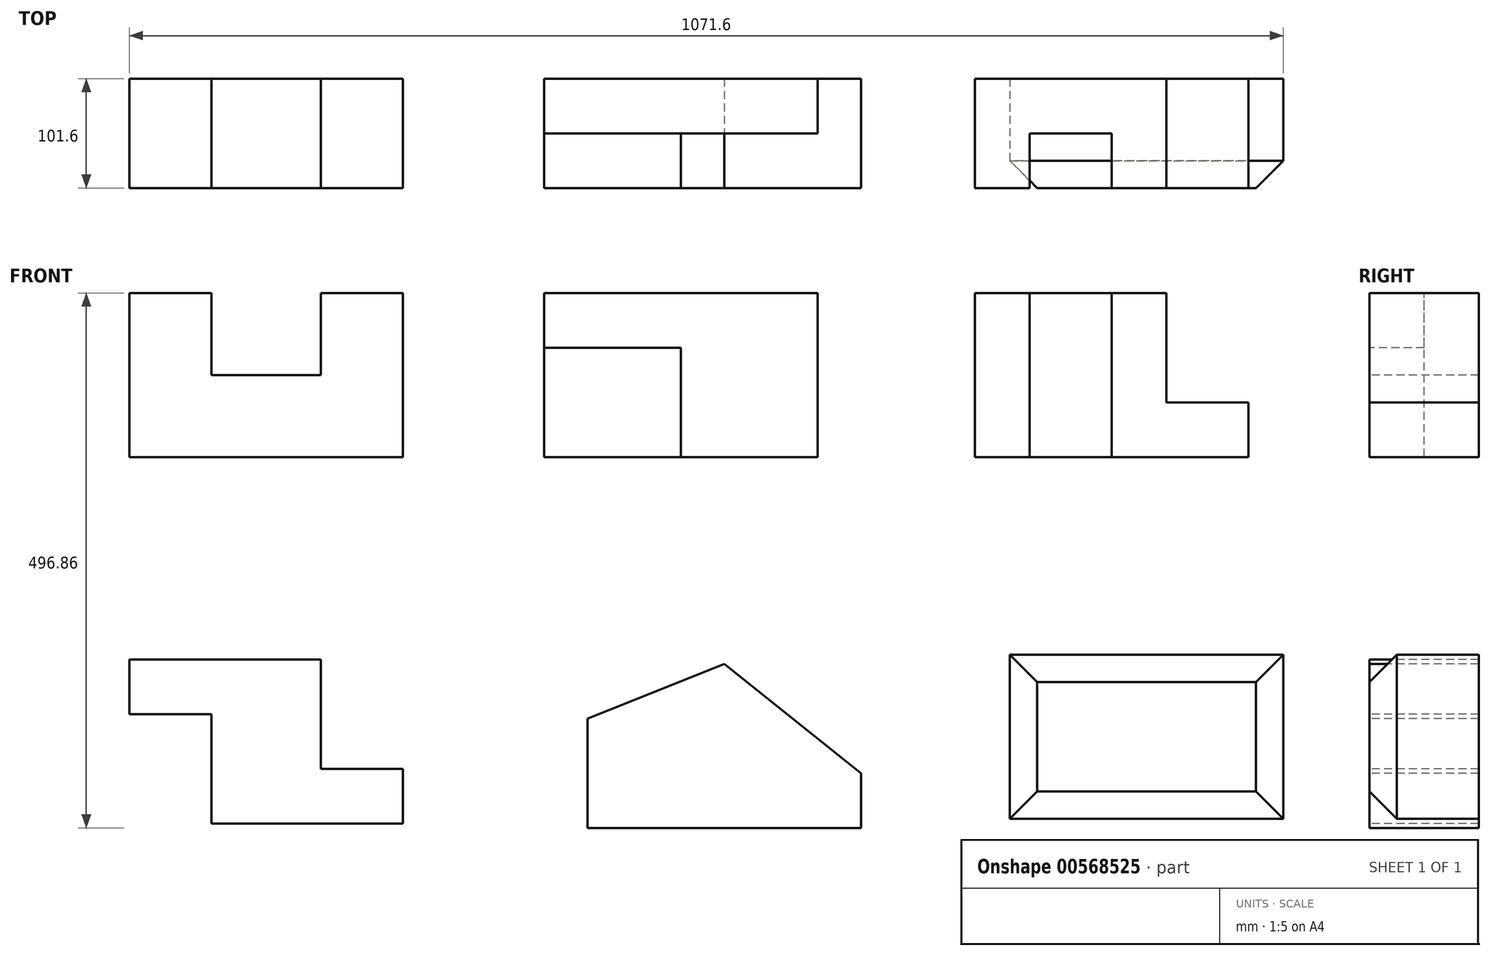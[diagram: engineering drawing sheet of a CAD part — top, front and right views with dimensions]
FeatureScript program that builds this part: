
annotation { "Feature Type Name" : "Feature", "Feature Type Description" : "" }
export const myFeature = defineFeature(function(context is Context, id is Id, definition is map)
    precondition{}
    {
        {
            var Q0;
            Q0=qCreatedBy(makeId("Front.planeOp"),FACE);
            var sketch = newSketch(context, id + "F0", { "sketchPlane" : qUnion([Q0])});
            skLineSegment(sketch, "E0", {"start": v(0, 0) * mm, "end": v(254, 0) * mm});
            skLineSegment(sketch, "E1", {"start": v(254, 0) * mm, "end": v(254, 152.4) * mm});
            skLineSegment(sketch, "E2", {"start": v(254, 152.4) * mm, "end": v(177.8, 152.4) * mm});
            skLineSegment(sketch, "E3", {"start": v(177.8, 152.4) * mm, "end": v(177.8, 76.2) * mm});
            skLineSegment(sketch, "E4", {"start": v(177.8, 76.2) * mm, "end": v(76.2, 76.2) * mm});
            skLineSegment(sketch, "E5", {"start": v(76.2, 76.2) * mm, "end": v(76.2, 152.4) * mm});
            skLineSegment(sketch, "E6", {"start": v(76.2, 152.4) * mm, "end": v(0, 152.4) * mm});
            skLineSegment(sketch, "E7", {"start": v(0, 152.4) * mm, "end": v(0, 0) * mm});
            skSolve(sketch);
        }
        {
            var Q0;
            Q0=makeQuery(id+"F0.imprint","IMPRINT",FACE,{"disambiguationData":[TD([[makeQuery(id+"F0.imprint","IMPRINT",EDGE,{"derivedFrom":sQuery(id+"F0.wireOp",EDGE,"E0")}),1.0]])]});
            extrude(context, id + "F1", {"entities" : qUnion([Q0]), "oppositeDirection" : true, "depth" : 101.6 * mm, "offsetDistance" : 25.4 * mm});
        }
        {
            var Q0;
            Q0=qCreatedBy(makeId("Front.planeOp"),FACE);
            var sketch = newSketch(context, id + "F2", { "sketchPlane" : qUnion([Q0])});
            skLineSegment(sketch, "E8.bottom", {"start": v(385.05, 0) * mm, "end": v(639.05, 0) * mm});
            skLineSegment(sketch, "E8.top", {"start": v(385.05, 152.4) * mm, "end": v(639.05, 152.4) * mm});
            skLineSegment(sketch, "E8.left", {"start": v(385.05, 0) * mm, "end": v(385.05, 152.4) * mm});
            skLineSegment(sketch, "E8.right", {"start": v(639.05, 0) * mm, "end": v(639.05, 152.4) * mm});
            skSolve(sketch);
        }
        {
            var Q0;
            Q0=makeQuery(id+"F2.imprint","IMPRINT",FACE,{"disambiguationData":[TD([[makeQuery(id+"F2.imprint","IMPRINT",EDGE,{"derivedFrom":sQuery(id+"F2.wireOp",EDGE,"E8.bottom")}),1.0]])]});
            extrude(context, id + "F3", {"entities" : qUnion([Q0]), "oppositeDirection" : true, "depth" : 101.6 * mm, "offsetDistance" : 25.4 * mm});
        }
        {
            var Q0;
            Q0=makeQuery(id+"F3.opExtrude","CAP_FACE",FACE,{"disambiguationData":[OSD([sQuery(id+"F2.wireOp",EDGE,"E8.bottom"),sQuery(id+"F2.wireOp",EDGE,"E8.top"),sQuery(id+"F2.wireOp",EDGE,"E8.left"),sQuery(id+"F2.wireOp",EDGE,"E8.right")])],"isStart":true});
            var sketch = newSketch(context, id + "F4", { "sketchPlane" : qUnion([Q0])});
            skLineSegment(sketch, "E9", {"start": v(512.05, 0) * mm, "end": v(512.05, 101.6) * mm});
            skLineSegment(sketch, "E10", {"start": v(512.05, 101.6) * mm, "end": v(385.05, 101.6) * mm});
            skSolve(sketch);
        }
        {
            var Q0;
            {var subQ3=sQuery(id+"F4.wireOp",EDGE,"E9");Q0=makeQuery(id+"F4.imprint","IMPRINT",FACE,{"disambiguationData":[TD([[makeQuery(id+"F4.imprint","IMPRINT",EDGE,{"derivedFrom":subQ3}),-1.0]])]});}
            extrude(context, id + "F5", {"entities" : qUnion([Q0]), "operationType" : NewBodyOperationType.REMOVE, "oppositeDirection" : true, "depth" : 50.8 * mm, "offsetDistance" : 25.4 * mm});
        }
        {
            var Q0;
            Q0=qCreatedBy(makeId("Front.planeOp"),FACE);
            var sketch = newSketch(context, id + "F6", { "sketchPlane" : qUnion([Q0])});
            skLineSegment(sketch, "E11.bottom", {"start": v(785.16, 0) * mm, "end": v(1039.16, 0) * mm});
            skLineSegment(sketch, "E11.top", {"start": v(785.16, 152.4) * mm, "end": v(1039.16, 152.4) * mm});
            skLineSegment(sketch, "E11.left", {"start": v(785.16, 0) * mm, "end": v(785.16, 152.4) * mm});
            skLineSegment(sketch, "E11.right", {"start": v(1039.16, 0) * mm, "end": v(1039.16, 152.4) * mm});
            skSolve(sketch);
        }
        {
            var Q0;
            Q0 = qSketchRegion(id + "F6", true);
            extrude(context, id + "F7", {"entities" : qUnion([Q0]), "oppositeDirection" : true, "depth" : 101.6 * mm, "offsetDistance" : 25.4 * mm});
        }
        {
            var Q0;
            Q0=makeQuery(id+"F7.opExtrude","CAP_FACE",FACE,{"disambiguationData":[OSD([sQuery(id+"F6.wireOp",EDGE,"E11.bottom"),sQuery(id+"F6.wireOp",EDGE,"E11.top"),sQuery(id+"F6.wireOp",EDGE,"E11.left"),sQuery(id+"F6.wireOp",EDGE,"E11.right")])],"isStart":true});
            var sketch = newSketch(context, id + "F8", { "sketchPlane" : qUnion([Q0])});
            skLineSegment(sketch, "E12", {"start": v(835.96, 0) * mm, "end": v(835.96, 152.4) * mm});
            skLineSegment(sketch, "E13", {"start": v(835.96, 152.4) * mm, "end": v(912.16, 152.4) * mm});
            skLineSegment(sketch, "E14", {"start": v(912.16, 152.4) * mm, "end": v(912.16, 0) * mm});
            skSolve(sketch);
        }
        {
            var Q0;
            {var subQ0=sQuery(id+"F8.wireOp",EDGE,"E12");Q0=makeQuery(id+"F8.imprint","IMPRINT",FACE,{"disambiguationData":[TD([[makeQuery(id+"F8.imprint","IMPRINT",EDGE,{"derivedFrom":subQ0}),-1.0]])]});}
            extrude(context, id + "F9", {"entities" : qUnion([Q0]), "operationType" : NewBodyOperationType.REMOVE, "oppositeDirection" : true, "depth" : 50.8 * mm, "offsetDistance" : 25.4 * mm});
        }
        {
            var Q0;
            {var subQ0=sQuery(id+"F6.wireOp",EDGE,"E11.bottom");var subQ1=sQuery(id+"F6.wireOp",EDGE,"E11.right");var subQ2=sQuery(id+"F6.wireOp",EDGE,"E11.top");Q0=makeQuery(id+"F9.boolean.opBoolean","SPLIT",FACE,{"disambiguationData":[TD([makeQuery(id+"F7.opExtrude","SWEPT_FACE",FACE,{"disambiguationData":[OSD([subQ1])]})])],"derivedFrom":makeQuery(id+"F7.opExtrude","CAP_FACE",FACE,{"disambiguationData":[OSD([subQ0,subQ2,sQuery(id+"F6.wireOp",EDGE,"E11.left"),subQ1])],"isStart":true})});}
            var sketch = newSketch(context, id + "F10", { "sketchPlane" : qUnion([Q0])});
            skLineSegment(sketch, "E15", {"start": v(1039.16, 152.4) * mm, "end": v(962.96, 152.4) * mm});
            skLineSegment(sketch, "E16", {"start": v(962.96, 152.4) * mm, "end": v(962.96, 50.8) * mm});
            skLineSegment(sketch, "E17", {"start": v(962.96, 50.8) * mm, "end": v(1039.16, 50.8) * mm});
            skSolve(sketch);
        }
        {
            var Q0;
            {var subQ0=sQuery(id+"F10.wireOp",EDGE,"E15");Q0=makeQuery(id+"F10.imprint","IMPRINT",FACE,{"disambiguationData":[TD([[makeQuery(id+"F10.imprint","IMPRINT",EDGE,{"derivedFrom":subQ0}),-1.0]])]});}
            extrude(context, id + "F11", {"entities" : qUnion([Q0]), "operationType" : NewBodyOperationType.REMOVE, "oppositeDirection" : true, "depth" : 167.64 * mm, "offsetDistance" : 25.4 * mm});
        }
        {
            var Q0;
            Q0=qCreatedBy(makeId("Front.planeOp"),FACE);
            var sketch = newSketch(context, id + "F12", { "sketchPlane" : qUnion([Q0])});
            skLineSegment(sketch, "E18.bottom", {"start": v(0, -340.48) * mm, "end": v(254, -340.48) * mm});
            skLineSegment(sketch, "E18.top", {"start": v(0, -188.08) * mm, "end": v(254, -188.08) * mm});
            skLineSegment(sketch, "E18.left", {"start": v(0, -340.48) * mm, "end": v(0, -188.08) * mm});
            skLineSegment(sketch, "E18.right", {"start": v(254, -340.48) * mm, "end": v(254, -188.08) * mm});
            skSolve(sketch);
        }
        {
            var Q0;
            Q0=makeQuery(id+"F12.imprint","IMPRINT",FACE,{"disambiguationData":[TD([[makeQuery(id+"F12.imprint","IMPRINT",EDGE,{"derivedFrom":sQuery(id+"F12.wireOp",EDGE,"E18.bottom")}),1.0]])]});
            extrude(context, id + "F13", {"entities" : qUnion([Q0]), "oppositeDirection" : true, "depth" : 101.6 * mm, "offsetDistance" : 25.4 * mm});
        }
        {
            var Q0;
            Q0=makeQuery(id+"F13.opExtrude","CAP_FACE",FACE,{"disambiguationData":[OSD([sQuery(id+"F12.wireOp",EDGE,"E18.bottom"),sQuery(id+"F12.wireOp",EDGE,"E18.top"),sQuery(id+"F12.wireOp",EDGE,"E18.left"),sQuery(id+"F12.wireOp",EDGE,"E18.right")])],"isStart":true});
            var sketch = newSketch(context, id + "F14", { "sketchPlane" : qUnion([Q0])});
            skLineSegment(sketch, "E19.bottom", {"start": v(0, -340.48) * mm, "end": v(76.2, -340.48) * mm});
            skLineSegment(sketch, "E19.top", {"start": v(0, -238.88) * mm, "end": v(76.2, -238.88) * mm});
            skLineSegment(sketch, "E19.left", {"start": v(0, -340.48) * mm, "end": v(0, -238.88) * mm});
            skLineSegment(sketch, "E19.right", {"start": v(76.2, -340.48) * mm, "end": v(76.2, -238.88) * mm});
            skSolve(sketch);
        }
        {
            var Q0;
            Q0=makeQuery(id+"F14.imprint","IMPRINT",FACE,{"disambiguationData":[TD([[makeQuery(id+"F14.imprint","IMPRINT",EDGE,{"derivedFrom":sQuery(id+"F14.wireOp",EDGE,"E19.bottom")}),1.0]])]});
            extrude(context, id + "F15", {"entities" : qUnion([Q0]), "operationType" : NewBodyOperationType.REMOVE, "oppositeDirection" : true, "depth" : 223.52 * mm, "offsetDistance" : 25.4 * mm});
        }
        {
            var Q0;
            Q0=makeQuery(id+"F13.opExtrude","CAP_FACE",FACE,{"disambiguationData":[OSD([sQuery(id+"F12.wireOp",EDGE,"E18.bottom"),sQuery(id+"F12.wireOp",EDGE,"E18.top"),sQuery(id+"F12.wireOp",EDGE,"E18.left"),sQuery(id+"F12.wireOp",EDGE,"E18.right")])],"isStart":true});
            var sketch = newSketch(context, id + "F16", { "sketchPlane" : qUnion([Q0])});
            skLineSegment(sketch, "E20.bottom", {"start": v(254, -188.08) * mm, "end": v(177.8, -188.08) * mm});
            skLineSegment(sketch, "E20.top", {"start": v(254, -289.68) * mm, "end": v(177.8, -289.68) * mm});
            skLineSegment(sketch, "E20.left", {"start": v(254, -188.08) * mm, "end": v(254, -289.68) * mm});
            skLineSegment(sketch, "E20.right", {"start": v(177.8, -188.08) * mm, "end": v(177.8, -289.68) * mm});
            skSolve(sketch);
        }
        {
            var Q0;
            Q0=makeQuery(id+"F16.imprint","IMPRINT",FACE,{"disambiguationData":[TD([[makeQuery(id+"F16.imprint","IMPRINT",EDGE,{"derivedFrom":sQuery(id+"F16.wireOp",EDGE,"E20.bottom")}),-1.0]])]});
            extrude(context, id + "F17", {"entities" : qUnion([Q0]), "operationType" : NewBodyOperationType.REMOVE, "oppositeDirection" : true, "depth" : 132.08 * mm, "offsetDistance" : 25.4 * mm});
        }
        {
            var Q0;
            Q0=qCreatedBy(makeId("Front.planeOp"),FACE);
            var sketch = newSketch(context, id + "F18", { "sketchPlane" : qUnion([Q0])});
            skLineSegment(sketch, "E21", {"start": v(425.47, -344.46) * mm, "end": v(425.47, -242.86) * mm});
            skLineSegment(sketch, "E22", {"start": v(425.47, -344.46) * mm, "end": v(679.47, -344.46) * mm});
            skLineSegment(sketch, "E23", {"start": v(679.47, -344.46) * mm, "end": v(679.47, -293.66) * mm});
            skLineSegment(sketch, "E24", {"start": v(552.47, -192.06) * mm, "end": v(425.47, -242.86) * mm});
            skLineSegment(sketch, "E25", {"start": v(552.47, -192.06) * mm, "end": v(679.47, -293.66) * mm});
            skSolve(sketch);
        }
        {
            var Q0;
            Q0=makeQuery(id+"F18.imprint","IMPRINT",FACE,{"disambiguationData":[TD([[makeQuery(id+"F18.imprint","IMPRINT",EDGE,{"derivedFrom":sQuery(id+"F18.wireOp",EDGE,"E21")}),-1.0]])]});
            extrude(context, id + "F19", {"entities" : qUnion([Q0]), "oppositeDirection" : true, "depth" : 101.6 * mm, "offsetDistance" : 25.4 * mm});
        }
        {
            var Q0;
            Q0=qCreatedBy(makeId("Front.planeOp"),FACE);
            var sketch = newSketch(context, id + "F20", { "sketchPlane" : qUnion([Q0])});
            skLineSegment(sketch, "E26.bottom", {"start": v(817.6, -335.94) * mm, "end": v(1071.6, -335.94) * mm});
            skLineSegment(sketch, "E26.top", {"start": v(817.6, -183.54) * mm, "end": v(1071.6, -183.54) * mm});
            skLineSegment(sketch, "E26.left", {"start": v(817.6, -335.94) * mm, "end": v(817.6, -183.54) * mm});
            skLineSegment(sketch, "E26.right", {"start": v(1071.6, -335.94) * mm, "end": v(1071.6, -183.54) * mm});
            skSolve(sketch);
        }
        {
            var Q0;
            Q0=makeQuery(id+"F20.imprint","IMPRINT",FACE,{"disambiguationData":[TD([[makeQuery(id+"F20.imprint","IMPRINT",EDGE,{"derivedFrom":sQuery(id+"F20.wireOp",EDGE,"E26.bottom")}),1.0]])]});
            extrude(context, id + "F21", {"entities" : qUnion([Q0]), "oppositeDirection" : true, "depth" : 101.6 * mm, "offsetDistance" : 25.4 * mm});
        }
        {
            var Q0;
            Q0=makeQuery(id+"F21.opExtrude","CAP_FACE",FACE,{"disambiguationData":[OSD([sQuery(id+"F20.wireOp",EDGE,"E26.bottom"),sQuery(id+"F20.wireOp",EDGE,"E26.top"),sQuery(id+"F20.wireOp",EDGE,"E26.left"),sQuery(id+"F20.wireOp",EDGE,"E26.right")])],"isStart":true});
            chamfer(context, id + "F22", {"entities" : qUnion([Q0]), "width" : 25.4 * mm, "tangentPropagation" : true});
        }
    });
